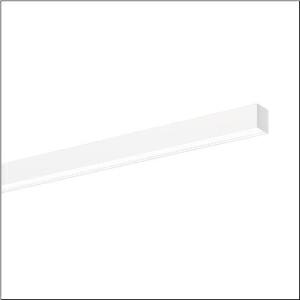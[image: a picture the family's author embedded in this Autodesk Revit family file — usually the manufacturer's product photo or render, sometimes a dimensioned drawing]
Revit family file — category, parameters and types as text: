
# Revit family: silica_r__21_51mx20tbt2w_71dc
name_source: partatom
category: Lighting Fixtures
units: mm (PartAtom-declared; Revit-internal decimal feet)

## family parameters
Cut with Voids When Loaded = No
Host = Face
Light Source = No
Part Type = Normal
Room Calculation Point = No
Round Connector Dimension = Use Diameter
Shared = No

## types (1)
- --- (1 x LED, 3000 lm, 25.6 W, 6500K)
    Apparent Load = 26 VA
    CIE Flux Codes = 48 79 96 100 100
    Color Rendering = 80
    Color Temperature = 6500K
    Default Elevation = 1800 mm
    Description = Silica® 21, office luminaire, primary optical cover: cover, of PMMA, opal, light emission: direct distribution, primary light characteristic: symmetric, installation type: surface-mounted, LED, rated luminous flux: 3.000lm, luminous efficacy: 112lm/W, light colour: 8tw, colour temperature: 2700..6500K, control gear: ECG DALI, with terminal, 3+2-pole, max. 2.5mm², mains connection: 220..240V, AC, 50/60Hz, rated input power: 26.9W, luminaire housing, of aluminium, traffic white (RAL 9016), length: 1.504mm, width: 53mm, height: 53mm, protection rating (complete): IP20, insulation class (complete): insulation class I (protective earthing), certification: CE, permissible operating ambient temperature: 0..+35°C, standard: EN 50419, packaging unit: 1 piece
    Height = 0 mm  [stored 0 ft]
    Lamp = 1 x LED
    Lamp Light Flux = 3000 lm
    Lamp Power = 25.6 W
    Lamp count = 1
    Length = 1504 mm
    Luminous efficacy = 117 lm/W
    Manufacturer = Siteco
    ModVariant = No
    Model = 51MX20TBT2W
    Mounting Place = Ceiling
    Mounting Type = Recessed
    Number of Poles = 1
    OnlyDefault = Yes
    Power Factor = 1
    Product Name = Silica® 21
    Product group = office luminaire | ceiling recessed
    ProductGroupID = 400
    Protection Class = Protection class I
    Protection Degree = IP 20
    RLX_Detail_Level = 1
    RLX_Emergency_Light_Flux = 0 lm
    RLX_Emergency_Type = 0
    RLX_Emergency_Type_DB = No
    RlxData = <blob elided: 20853 chars, md5=e03b5935>
    Socket = socket
    Standby Power = 0 W
    System Light Flux = 3000 lm
    System Power = 26 W
    Type Comments = individual setting
    Type Image = l_1335877.jpg
    URL = http://relux.com
    VarID = @adj_109507
    Voltage = 0 V
    Weight = 0.00 kg
    Width = 53 mm

note: [stored X ft] marks values corroborated as IEEE doubles in the binary element streams (Revit-internal decimal feet)

## geometry (parser evidence)
native form markers: Blend x4, Sweep x11
no freeform markers — native parametric forms only
